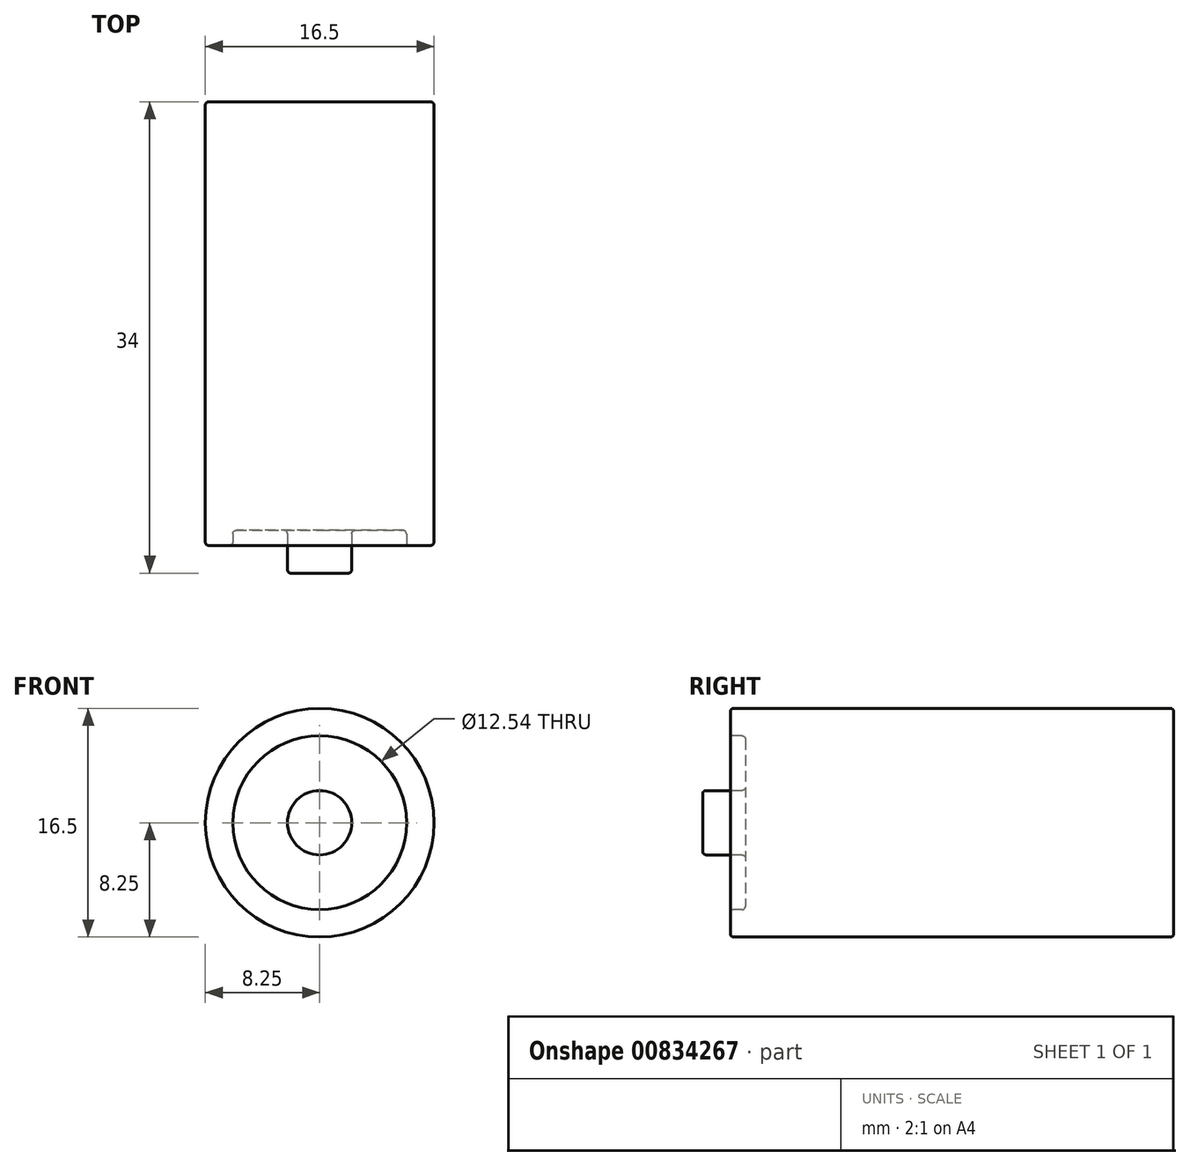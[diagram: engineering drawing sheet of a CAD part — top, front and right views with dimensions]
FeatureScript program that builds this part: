
annotation { "Feature Type Name" : "Feature", "Feature Type Description" : "" }
export const myFeature = defineFeature(function(context is Context, id is Id, definition is map)
    precondition{}
    {
        {
            var Q0;
            Q0=qCreatedBy(makeId("Top.planeOp"),FACE);
            var sketch = newSketch(context, id + "F0", { "sketchPlane" : qUnion([Q0])});
            skLineSegment(sketch, "E0", {"start": v(0, 24.13) * mm, "end": v(8.25, 24.13) * mm});
            skLineSegment(sketch, "E1", {"start": v(8.25, 24.13) * mm, "end": v(8.25, -7.87) * mm});
            skLineSegment(sketch, "E2", {"start": v(8.25, -7.87) * mm, "end": v(6.27, -7.87) * mm});
            skLineSegment(sketch, "E3", {"start": v(6.27, -7.87) * mm, "end": v(6.27, -6.78) * mm});
            skLineSegment(sketch, "E4", {"start": v(6.27, -6.78) * mm, "end": v(2.32, -6.78) * mm});
            skLineSegment(sketch, "E5", {"start": v(2.32, -6.78) * mm, "end": v(2.32, -9.87) * mm});
            skLineSegment(sketch, "E6", {"start": v(2.32, -9.87) * mm, "end": v(0, -9.87) * mm});
            skLineSegment(sketch, "E7", {"start": v(0, -9.87) * mm, "end": v(0, 24.13) * mm});
            skSolve(sketch);
        }
        {
            var Q0;
            Q0=makeQuery(id+"F0.imprint","IMPRINT",FACE,{"disambiguationData":[TD([[makeQuery(id+"F0.imprint","IMPRINT",EDGE,{"derivedFrom":sQuery(id+"F0.wireOp",EDGE,"E0")}),-1.0]])]});
            var Q1;
            Q1=sQuery(id+"F0.wireOp",EDGE,"E7");
            revolve(context, id + "F1", {"surfaceOperationType" : NewSurfaceOperationType.NEW, "entities" : qUnion([Q0]), "axis" : qUnion([Q1]), "revolveType" : RevolveType.FULL});
        }
        {
            var Q0;
            Q0=makeQuery(id+"F1.opRevolve","SWEPT_EDGE",EDGE,{"disambiguationData":[OSD([sQuery(id+"F0.wireOp",EDGE,"E0"),sQuery(id+"F0.wireOp",EDGE,"E1")])]});
            var Q1;
            Q1=makeQuery(id+"F1.opRevolve","SWEPT_EDGE",EDGE,{"disambiguationData":[OSD([sQuery(id+"F0.wireOp",EDGE,"E1"),sQuery(id+"F0.wireOp",EDGE,"E2")])]});
            var Q2;
            Q2=makeQuery(id+"F1.opRevolve","SWEPT_EDGE",EDGE,{"disambiguationData":[OSD([sQuery(id+"F0.wireOp",EDGE,"E2"),sQuery(id+"F0.wireOp",EDGE,"E3")])]});
            var Q3;
            Q3=makeQuery(id+"F1.opRevolve","SWEPT_EDGE",EDGE,{"disambiguationData":[OSD([sQuery(id+"F0.wireOp",EDGE,"E3"),sQuery(id+"F0.wireOp",EDGE,"E4")])]});
            var Q4;
            Q4=makeQuery(id+"F1.opRevolve","SWEPT_EDGE",EDGE,{"disambiguationData":[OSD([sQuery(id+"F0.wireOp",EDGE,"E4"),sQuery(id+"F0.wireOp",EDGE,"E5")])]});
            var Q5;
            Q5=makeQuery(id+"F1.opRevolve","SWEPT_EDGE",EDGE,{"disambiguationData":[OSD([sQuery(id+"F0.wireOp",EDGE,"E5"),sQuery(id+"F0.wireOp",EDGE,"E6")])]});
            fillet(context, id + "F2", {"entities" : qUnion([Q0, Q1, Q2, Q3, Q4, Q5]), "radius" : .25 * mm, "tangentPropagation" : true, "allowEdgeOverflow" : false});
        }
    });
